# Revit family: Sanext_Термостатическая головка SANEXT TH
name_source: partatom
category: Арматура трубопроводов
revit_build: Autodesk Revit 2017 (Build: 20171027_0315(x64)
units: mm (PartAtom-declared; Revit-internal decimal feet)

## family parameters
Всегда вертикально = Да
На основе рабочей плоскости = Нет
Общий = Да
При загрузке вырезать с полостями = Нет
Размер круглого соединителя = Использовать радиус
Тип детали = Вставляется

## types (1)
- Sanext_Термостатическая головка SANEXT TH
    ADSK_Единица измерения = шт
    ADSK_Завод-изготовитель = ООО САНЕКСТ.ПРО
    ADSK_Код изделия = 6901
    ADSK_Марка = M 30x1.5
    ADSK_Масса = 0
    ADSK_Материал наименование = РВК_Полипропилен PPR
    ADSK_Наименование = Термостатическая головка SANEXT TH
    ADSK_Обозначение = M 30x1.5
    URL = http://sanext.ru
    h = 90 мм
    z = 0
    Изготовитель = ООО САНЕКСТ.ПРО
    Ключевая пометка = Термостатическая головка SANEXT TH
    Комментарии к типоразмеру = M 30x1.5
    Материал корпуса = РВК_Полипропилен PPR
    Описание = Термостатическая головка SANEXT TH
    Рабочее давление = 0.0 кПа
    Разработчик = ООО ПРОРУБИМ
    Разработчик (телефон) = +7(495)649-85-43
    Разработчик модели (URL) = http://prorubim.com
